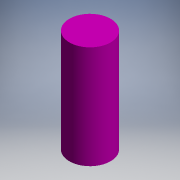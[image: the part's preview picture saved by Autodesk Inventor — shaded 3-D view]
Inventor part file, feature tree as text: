
AUTODESK INVENTOR PART (.ipt)
format: ipt  version: 2017 (Build 210142000, 142)  size: 73,216 bytes
history: native  units: mm (DEFAULTED — no unit token found)
features: extrude x1, sketch x1
ambient origin geometry x8: Origin, YZ Plane, XZ Plane, XY Plane, X Axis, Y Axis, Z Axis, Center Point
bodies: Solid1 (feature_tree)
feature tree (2):
  extrude  "Extrusion1"  [1 undecoded]
  sketch  "Sketch1"  dims[d2=0.0mm]
note: 1 required parameter value undecoded (feature->parameter linkage not recoverable at this tier; creation-order binding heuristic only, values carry confidence <= 0.55)
